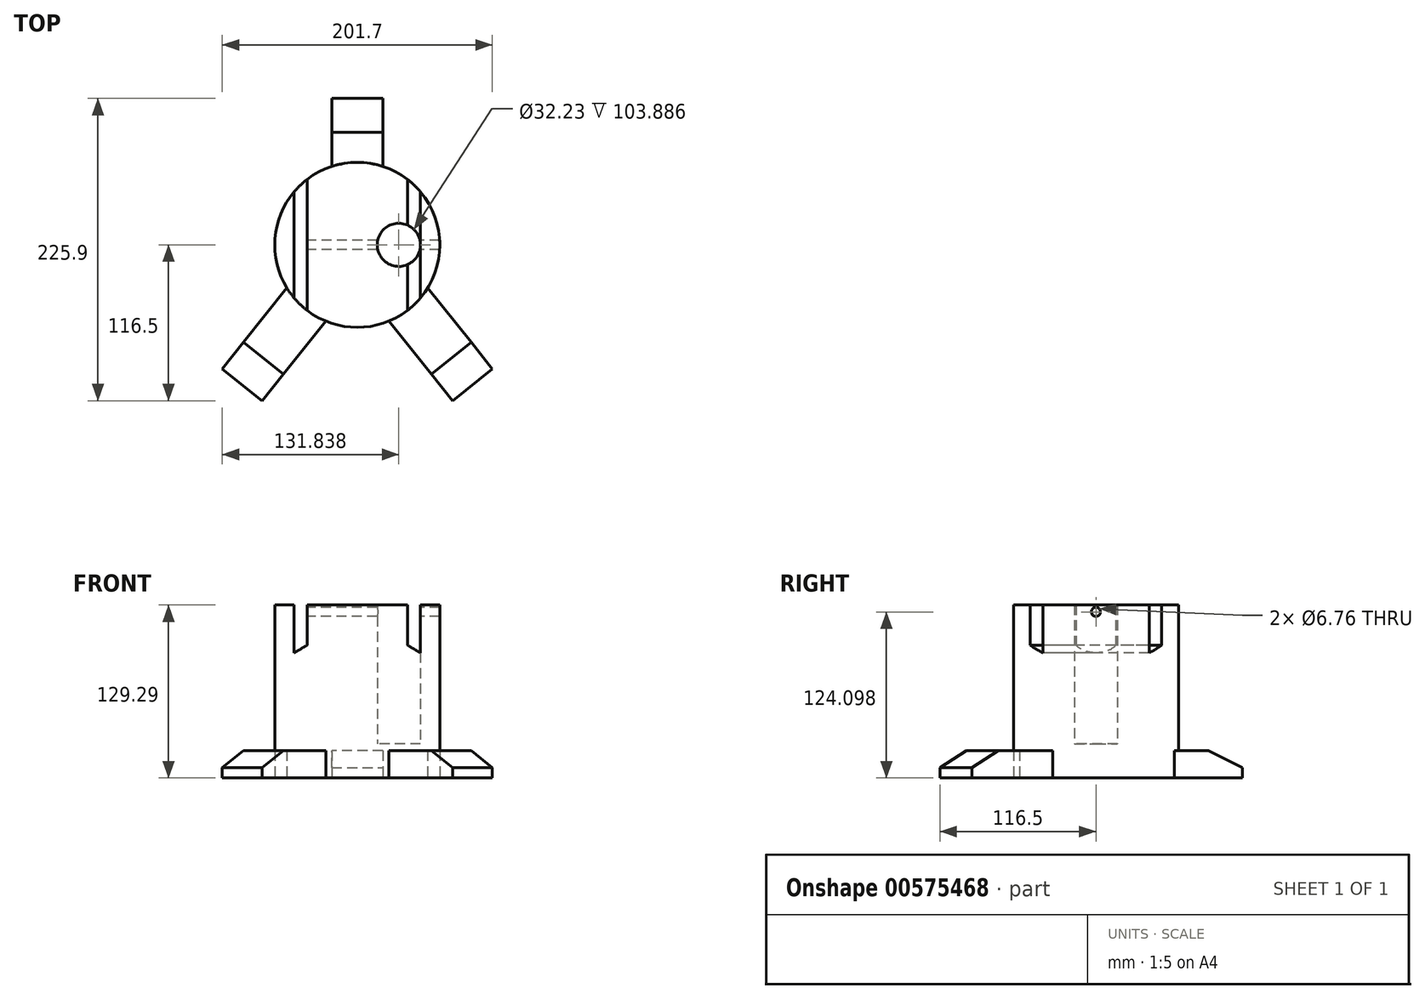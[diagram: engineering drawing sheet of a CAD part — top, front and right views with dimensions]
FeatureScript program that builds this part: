
annotation { "Feature Type Name" : "Feature", "Feature Type Description" : "" }
export const myFeature = defineFeature(function(context is Context, id is Id, definition is map)
    precondition{}
    {
        {
            var Q0;
            Q0=qCreatedBy(makeId("Top.planeOp"),FACE);
            var sketch = newSketch(context, id + "F0", { "sketchPlane" : qUnion([Q0])});
            skCircle(sketch, "E0", {"center": v(0, 0) * mm, "radius": 61.62 * mm});
            skLineSegment(sketch, "E1", {"start": v(-23.53, -56.95) * mm, "end": v(-71.07, -116.5) * mm});
            skLineSegment(sketch, "E2", {"start": v(-71.07, -116.5) * mm, "end": v(-100.85, -92.73) * mm});
            skLineSegment(sketch, "E3", {"start": v(-100.85, -92.73) * mm, "end": v(-52.53, -32.22) * mm});
            skLineSegment(sketch, "E4", {"start": v(-19.05, 109.4) * mm, "end": v(19.05, 109.4) * mm});
            skLineSegment(sketch, "E5", {"start": v(19.05, 109.4) * mm, "end": v(19.05, 58.6) * mm});
            skLineSegment(sketch, "E6", {"start": v(-19.05, 109.4) * mm, "end": v(-19.05, 58.6) * mm});
            skLineSegment(sketch, "E7.MirrorCS", {"start": v(100.85, -92.73) * mm, "end": v(52.53, -32.22) * mm});
            skLineSegment(sketch, "E8.MirrorCS", {"start": v(23.53, -56.95) * mm, "end": v(71.07, -116.5) * mm});
            skLineSegment(sketch, "E9.MirrorCS", {"start": v(71.07, -116.5) * mm, "end": v(100.85, -92.73) * mm});
            skSolve(sketch);
        }
        {
            var Q0;
            {var subQ0=sQuery(id+"F0.wireOp",EDGE,"E0");var subQ5=makeQuery(id+"F0.imprint","INTERSECT",VERTEX,{"derivedFrom":[subQ0,sQuery(id+"F0.wireOp",EDGE,"E5")]});Q0=makeQuery(id+"F0.imprint","IMPRINT",FACE,{"disambiguationData":[TD([[makeQuery(id+"F0.imprint","IMPRINT",EDGE,{"disambiguationData":[TD([[subQ5,-1.0]])],"derivedFrom":subQ0}),1.0]])]});}
            extrude(context, id + "F1", {"entities" : qUnion([Q0]), "depth" : 25.4 * mm, "offsetDistance" : 25.4 * mm});
        }
        {
            var Q0;
            {var subQ0=sQuery(id+"F0.wireOp",EDGE,"E1");Q0=makeQuery(id+"F0.imprint","IMPRINT",FACE,{"disambiguationData":[TD([[makeQuery(id+"F0.imprint","IMPRINT",EDGE,{"derivedFrom":subQ0}),-1.0]])]});}
            var Q1;
            Q1=makeQuery(id+"F0.imprint","IMPRINT",FACE,{"disambiguationData":[TD([[makeQuery(id+"F0.imprint","IMPRINT",EDGE,{"derivedFrom":sQuery(id+"F0.wireOp",EDGE,"E4")}),-1.0]])]});
            var Q2;
            {var subQ0=sQuery(id+"F0.wireOp",EDGE,"E7.MirrorCS");Q2=makeQuery(id+"F0.imprint","IMPRINT",FACE,{"disambiguationData":[TD([[makeQuery(id+"F0.imprint","IMPRINT",EDGE,{"derivedFrom":subQ0}),1.0]])]});}
            extrude(context, id + "F2", {"entities" : qUnion([Q0, Q1, Q2]), "operationType" : NewBodyOperationType.ADD, "depth" : 20.32 * mm, "offsetDistance" : 25.4 * mm});
        }
        {
            var Q0;
            Q0=makeQuery(id+"F2.opExtrude","CAP_EDGE",EDGE,{"disambiguationData":[OSD([sQuery(id+"F0.wireOp",EDGE,"E9.MirrorCS")])],"isStart":false});
            chamfer(context, id + "F3", {"entities" : qUnion([Q0]), "chamferType" : ChamferType.TWO_OFFSETS, "width1" : 25.4 * mm, "oppositeDirection" : false, "width2" : 12.7 * mm, "tangentPropagation" : true});
        }
        {
            var Q0;
            Q0=makeQuery(id+"F2.opExtrude","CAP_EDGE",EDGE,{"disambiguationData":[OSD([sQuery(id+"F0.wireOp",EDGE,"E2")])],"isStart":false});
            var Q1;
            Q1=makeQuery(id+"F2.opExtrude","CAP_EDGE",EDGE,{"disambiguationData":[OSD([sQuery(id+"F0.wireOp",EDGE,"E4")])],"isStart":false});
            chamfer(context, id + "F4", {"entities" : qUnion([Q0, Q1]), "chamferType" : ChamferType.TWO_OFFSETS, "width1" : 12.7 * mm, "oppositeDirection" : false, "width2" : 25.4 * mm, "tangentPropagation" : true});
        }
        {
            var Q0;
            Q0=makeQuery(id+"F1.opExtrude","CAP_FACE",FACE,{"disambiguationData":[OSD([sQuery(id+"F0.wireOp",EDGE,"E0"),sQuery(id+"F0.wireOp",EDGE,"DcNjS8cu-issq-BmN7-eNk9-ciyLhwBEdFtM")])],"isStart":false});
            var sketch = newSketch(context, id + "F5", { "sketchPlane" : qUnion([Q0])});
            skLineSegment(sketch, "E10", {"start": v(-61.62, 0) * mm, "end": v(61.62, 0) * mm, "construction": true});
            skLineSegment(sketch, "E11", {"start": v(0, 61.62) * mm, "end": v(0, -61.62) * mm, "construction": true});
            skCircle(sketch, "E12", {"center": v(-30.99, 0) * mm, "radius": 16.11 * mm});
            skCircle(sketch, "E13.MirrorC", {"center": v(30.99, 0) * mm, "radius": 16.11 * mm});
            skSolve(sketch);
        }
        {
            var Q0;
            Q0=makeQuery(id+"F5.imprint","IMPRINT",FACE,{"disambiguationData":[TD([[makeQuery(id+"F5.imprint","IMPRINT",EDGE,{"derivedFrom":sQuery(id+"F5.wireOp",EDGE,"E12")}),1.0]])]});
            var Q1;
            Q1=makeQuery(id+"F5.imprint","IMPRINT",FACE,{"disambiguationData":[TD([[makeQuery(id+"F5.imprint","IMPRINT",EDGE,{"derivedFrom":sQuery(id+"F5.wireOp",EDGE,"E13.MirrorC")}),-1.0]])]});
            extrude(context, id + "F6", {"entities" : qUnion([Q0, Q1]), "operationType" : NewBodyOperationType.ADD, "depth" : 103.89 * mm, "offsetDistance" : 25.4 * mm});
        }
        {
            var Q0;
            Q0=qCreatedBy(makeId("Front.planeOp"),FACE);
            var sketch = newSketch(context, id + "F7", { "sketchPlane" : qUnion([Q0])});
            skLineSegment(sketch, "E14", {"start": v(-47.1, 25.4) * mm, "end": v(-47.1, 129.29) * mm});
            skLineSegment(sketch, "E15", {"start": v(-14.87, 129.29) * mm, "end": v(-14.87, 25.4) * mm});
            skLineSegment(sketch, "E16.0", {"start": v(-47.1, 129.29) * mm, "end": v(-14.87, 129.29) * mm});
            skLineSegment(sketch, "E17", {"start": v(14.87, 25.4) * mm, "end": v(14.87, 129.29) * mm});
            skLineSegment(sketch, "E18.0", {"start": v(47.1, 129.29) * mm, "end": v(14.87, 129.29) * mm});
            skLineSegment(sketch, "E19", {"start": v(47.1, 129.29) * mm, "end": v(47.1, 25.4) * mm});
            skLineSegment(sketch, "E20", {"start": v(-37.4, 129.29) * mm, "end": v(-37.4, 99.25) * mm});
            skLineSegment(sketch, "E21", {"start": v(-37.4, 99.25) * mm, "end": v(-47.1, 93.57) * mm});
            skLineSegment(sketch, "E22", {"start": v(-14.87, 129.29) * mm, "end": v(14.87, 129.29) * mm});
            skLineSegment(sketch, "E23", {"start": v(0, 129.29) * mm, "end": v(0, 73.9) * mm});
            skPoint(sketch, "E23.endSnap0", {"position": v(0, 129.29) * mm});
            skLineSegment(sketch, "E24.MirrorCS", {"start": v(37.4, 129.29) * mm, "end": v(37.4, 99.25) * mm});
            skLineSegment(sketch, "E25.MirrorCS", {"start": v(37.4, 99.25) * mm, "end": v(47.1, 93.57) * mm});
            skSolve(sketch);
        }
        {
            var Q0;
            Q0 = qSketchRegion(id + "F7", true);
            extrude(context, id + "F8", {"entities" : qUnion([Q0]), "operationType" : NewBodyOperationType.REMOVE, "endBound" : BoundingType.THROUGH_ALL, "oppositeDirection" : true, "depth" : 25.4 * mm, "offsetDistance" : 25.4 * mm, "hasSecondDirection" : true, "secondDirectionBound" : SecondDirectionBoundingType.THROUGH_ALL, "secondDirectionOppositeDirection" : false, "secondDirectionDepth" : 25.4 * mm});
        }
        {
            var Q0;
            Q0=makeQuery(id+"F8.boolean.opBoolean","COPY",FACE,{"derivedFrom":makeQuery(id+"F8.opExtrude","SWEPT_FACE",FACE,{"disambiguationData":[OSD([sQuery(id+"F7.wireOp",EDGE,"E20")])]})});
            var sketch = newSketch(context, id + "F9", { "sketchPlane" : qUnion([Q0])});
            skCircle(sketch, "E26", {"center": v(0, 124.1) * mm, "radius": 3.38 * mm});
            skSolve(sketch);
        }
        {
            var Q0;
            Q0=makeQuery(id+"F9.imprint","IMPRINT",FACE,{"disambiguationData":[TD([[makeQuery(id+"F9.imprint","IMPRINT",EDGE,{"derivedFrom":sQuery(id+"F9.wireOp",EDGE,"E26")}),1.0]])]});
            extrude(context, id + "F10", {"entities" : qUnion([Q0]), "operationType" : NewBodyOperationType.REMOVE, "endBound" : BoundingType.THROUGH_ALL, "oppositeDirection" : true, "depth" : 25.4 * mm, "offsetDistance" : 25.4 * mm});
        }
    });
